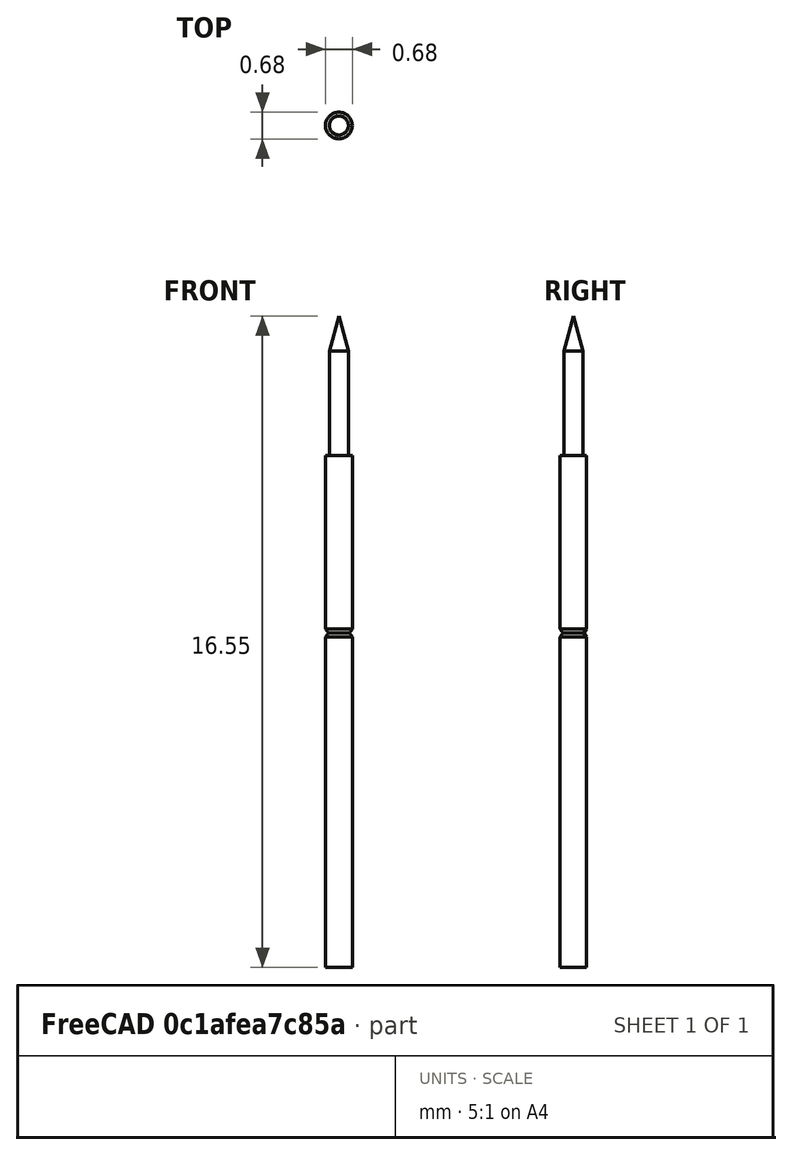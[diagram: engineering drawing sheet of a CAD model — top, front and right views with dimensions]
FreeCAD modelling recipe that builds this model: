
FCSTD DOCUMENT  (FreeCAD 0.19R23141 (Git))
Label: P50-B1_pogo
License: All rights reserved
LicenseURL: http://en.wikipedia.org/wiki/All_rights_reserved
objects: Sketcher::SketchObject×1, PartDesign::Revolution×1, PartDesign::Body×1
note: 4 computed .brp shape members not serialized (recipe doc carries the construction recipe); baked Part::Feature solids carry a one-line shape summary decoded from their .brp

FEATURE [Sketcher::SketchObject] Sketch
  MapMode = 5
  Placement = pos=(0,0,0) rot=(1,0,0;1.5708rad)
  Support = -> [XZ_Plane]
  sketch-geometry (10):
    g0: LineSegment StartX=0 StartY=0 StartZ=0 EndX=-0.34 EndY=0 EndZ=0
    g1: LineSegment [constr] StartX=-0.34 StartY=0 StartZ=0 EndX=-0.34 EndY=13 EndZ=0
    g2: LineSegment StartX=-0.34 StartY=13 StartZ=0 EndX=-0.24 EndY=13 EndZ=0
    g3: LineSegment StartX=-0.24 StartY=13 StartZ=0 EndX=-0.24 EndY=15.6543 EndZ=0
    g4: LineSegment StartX=-0.24 StartY=15.6543 StartZ=0 EndX=0 EndY=16.55 EndZ=0
    g5: LineSegment StartX=0 StartY=0 StartZ=0 EndX=0 EndY=16.55 EndZ=0
    g6: LineSegment StartX=-0.34 StartY=13 StartZ=0 EndX=-0.34 EndY=8.6 EndZ=0
    g7: LineSegment StartX=-0.34 StartY=8.6 StartZ=0 EndX=-0.265 EndY=8.5 EndZ=0
    g8: LineSegment StartX=-0.265 StartY=8.5 StartZ=0 EndX=-0.34 EndY=8.4 EndZ=0
    g9: LineSegment StartX=-0.34 StartY=8.4 StartZ=0 EndX=-0.34 EndY=0 EndZ=0
  constraints (28):
    c: Coincident(g-1,g0)
    c: Coincident(g0,g1)
    c: PointOnObject(g0,g-1)
    c: DistanceX(g0,g0) = 0.34
    c: Vertical(g1)
    c: DistanceY(g1,g1) = 13
    c: Coincident(g1,g2)
    c: Coincident(g2,g3)
    c: Vertical(g3)
    c: Horizontal(g2)
    c: DistanceX(g2,g0) = 0.24
    c: Coincident(g4,g3)
    c: PointOnObject(g4,g-2)
    c: Angle(g4,g-2) = 0.261799
    c: DistanceY(g2,g4) = 3.55
    c: Coincident(g5,g0)
    c: Coincident(g5,g4)
    c: Coincident(g2,g6)
    c: PointOnObject(g6,g1)
    c: Coincident(g6,g7)
    c: Coincident(g7,g8)
    c: PointOnObject(g8,g1)
    c: Coincident(g8,g9)
    c: Coincident(g9,g0)
    c: Equal(g7,g8)
    c: DistanceY(g8,g6) = 0.2
    c: DistanceX(g6,g7) = 0.075
    c: DistanceY(g7,g2) = 4.5
FEATURE [PartDesign::Revolution] Revolution
  Angle = 360
  Axis = (0,2e-16,1)
  Base = (0,0,0)
  Placement = pos=(0,0,0) rot=(1,0,0;1.5708rad)
  Profile = -> Sketch
  ReferenceAxis = -> Sketch [V_Axis]
FEATURE [PartDesign::Body] Body
  Group = -> [Sketch,Revolution]
  Origin = -> Origin
  Tip = -> Revolution
